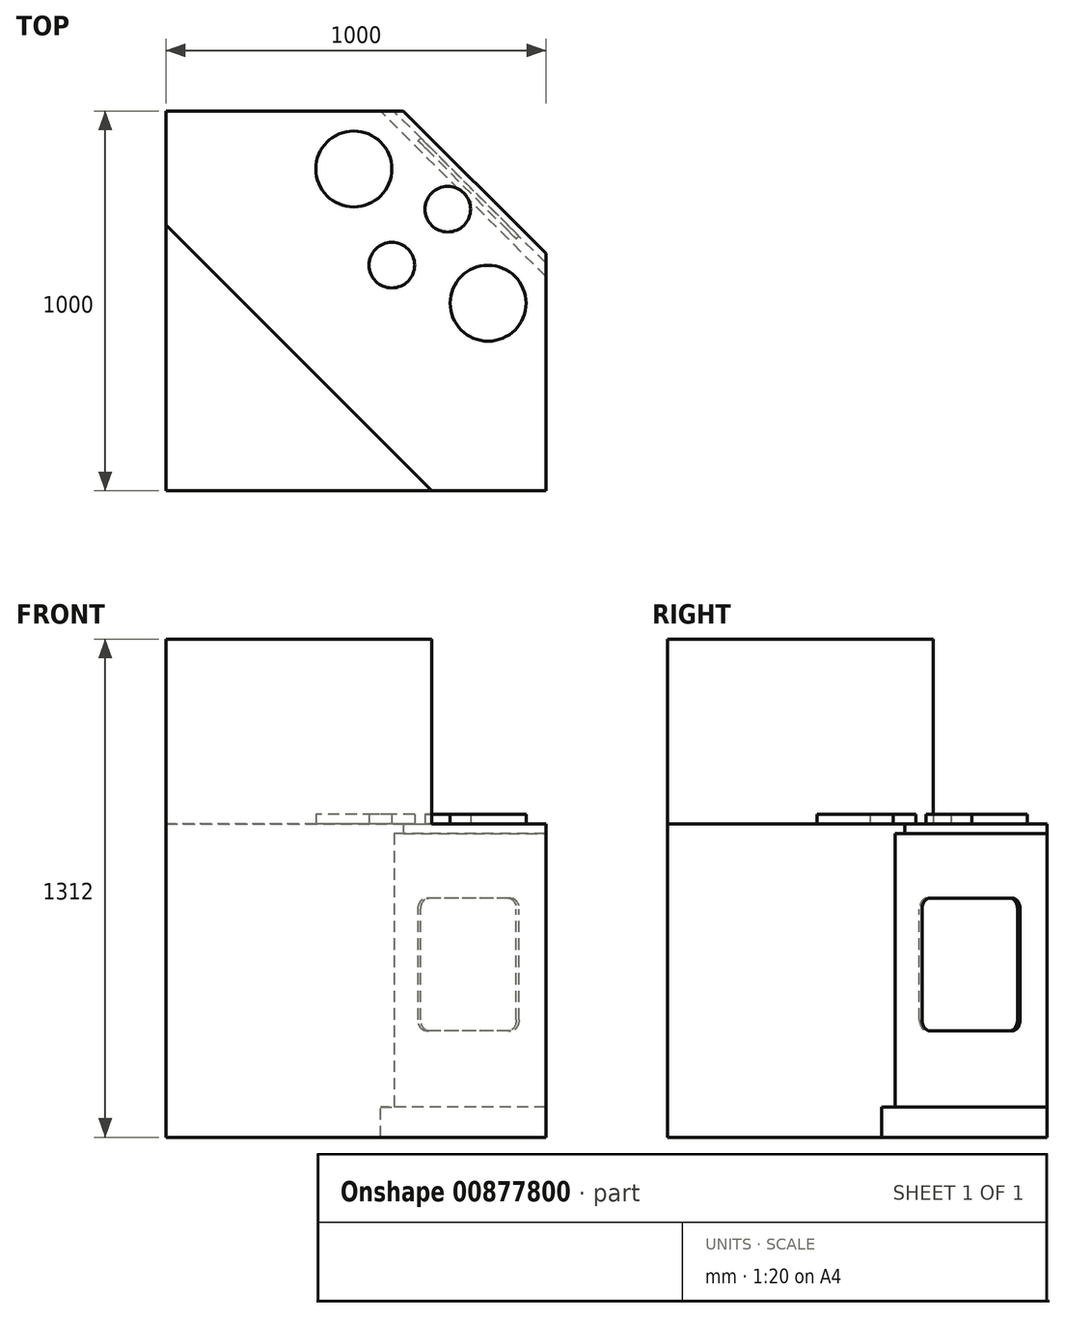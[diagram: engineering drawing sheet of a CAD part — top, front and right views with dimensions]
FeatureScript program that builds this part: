
annotation { "Feature Type Name" : "Feature", "Feature Type Description" : "" }
export const myFeature = defineFeature(function(context is Context, id is Id, definition is map)
    precondition{}
    {
        {
            var Q0;
            Q0=qCreatedBy(makeId("Top.planeOp"),FACE);
            var sketch = newSketch(context, id + "F0", { "sketchPlane" : qUnion([Q0])});
            skLineSegment(sketch, "E0.bottom", {"start": v(-500, -500) * mm, "end": v(500, -500) * mm});
            skLineSegment(sketch, "E0.left", {"start": v(-500, -500) * mm, "end": v(-500, 500) * mm});
            skPoint(sketch, "E0.middle", {"position": v(0, 0) * mm});
            skLineSegment(sketch, "E1", {"start": v(500, 100) * mm, "end": v(100, 500) * mm});
            skLineSegment(sketch, "E2", {"start": v(100, 500) * mm, "end": v(-500, 500) * mm});
            skLineSegment(sketch, "E3", {"start": v(500, 100) * mm, "end": v(500, -500) * mm});
            skSolve(sketch);
        }
        {
            var Q0;
            Q0 = qSketchRegion(id + "F0", true);
            extrude(context, id + "F1", {"entities" : qUnion([Q0]), "depth" : 800 * mm, "offsetDistance" : 25 * mm});
        }
        {
            var Q0;
            Q0=makeQuery(id+"F1.opExtrude","CAP_FACE",FACE,{"disambiguationData":[OSD([sQuery(id+"F0.wireOp",EDGE,"E0.bottom"),sQuery(id+"F0.wireOp",EDGE,"E0.left"),sQuery(id+"F0.wireOp",EDGE,"E1"),sQuery(id+"F0.wireOp",EDGE,"E2"),sQuery(id+"F0.wireOp",EDGE,"E3")])],"isStart":false});
            var sketch = newSketch(context, id + "F2", { "sketchPlane" : qUnion([Q0])});
            skLineSegment(sketch, "E4.bottom", {"start": v(-500, -500) * mm, "end": v(500, -500) * mm});
            skLineSegment(sketch, "E4.left", {"start": v(-500, -500) * mm, "end": v(-500, 500) * mm});
            skPoint(sketch, "E5", {"position": v(500, 125) * mm});
            skPoint(sketch, "E6", {"position": v(125, 500) * mm});
            skLineSegment(sketch, "E7", {"start": v(125, 500) * mm, "end": v(500, 125) * mm});
            skLineSegment(sketch, "E8", {"start": v(500, -500) * mm, "end": v(500, 125) * mm});
            skLineSegment(sketch, "E9", {"start": v(125, 500) * mm, "end": v(-500, 500) * mm});
            skSolve(sketch);
        }
        {
            var Q0;
            Q0 = qSketchRegion(id + "F2", true);
            extrude(context, id + "F3", {"entities" : qUnion([Q0]), "operationType" : NewBodyOperationType.ADD, "depth" : 25 * mm, "offsetDistance" : 25 * mm});
        }
        {
            var Q0;
            Q0=makeQuery(id+"F1.opExtrude","SWEPT_FACE",FACE,{"disambiguationData":[OSD([sQuery(id+"F0.wireOp",EDGE,"E1")])]});
            var sketch = newSketch(context, id + "F4", { "sketchPlane" : qUnion([Q0])});
            skLineSegment(sketch, "E10.bottom", {"start": v(-494.64, 0) * mm, "end": v(761.05, 0) * mm});
            skLineSegment(sketch, "E10.top", {"start": v(-494.64, 80) * mm, "end": v(761.05, 80) * mm});
            skLineSegment(sketch, "E10.left", {"start": v(-494.64, 0) * mm, "end": v(-494.64, 80) * mm});
            skLineSegment(sketch, "E10.right", {"start": v(761.05, 0) * mm, "end": v(761.05, 80) * mm});
            skSolve(sketch);
        }
        {
            var Q0;
            Q0 = qSketchRegion(id + "F4", true);
            extrude(context, id + "F5", {"entities" : qUnion([Q0]), "operationType" : NewBodyOperationType.REMOVE, "oppositeDirection" : true, "depth" : 25 * mm, "offsetDistance" : 25 * mm});
        }
        {
            var Q0;
            Q0=makeQuery(id+"F3.opExtrude","CAP_FACE",FACE,{"disambiguationData":[OSD([sQuery(id+"F2.wireOp",EDGE,"E4.bottom"),sQuery(id+"F2.wireOp",EDGE,"E4.left"),sQuery(id+"F2.wireOp",EDGE,"E7"),sQuery(id+"F2.wireOp",EDGE,"E8"),sQuery(id+"F2.wireOp",EDGE,"E9")])],"isStart":false});
            var sketch = newSketch(context, id + "F6", { "sketchPlane" : qUnion([Q0])});
            skCircle(sketch, "E11", {"center": v(241.79, 241.79) * mm, "radius": 60 * mm});
            skCircle(sketch, "E12", {"center": v(94.47, 94.47) * mm, "radius": 60 * mm});
            skCircle(sketch, "E13", {"center": v(347.86, -5.7) * mm, "radius": 100 * mm});
            skCircle(sketch, "E14", {"center": v(-5.7, 347.86) * mm, "radius": 100 * mm});
            skLineSegment(sketch, "E15", {"start": v(-500, -500) * mm, "end": v(312.5, 312.5) * mm, "construction": true});
            skSolve(sketch);
        }
        {
            var Q0;
            Q0 = qSketchRegion(id + "F6", true);
            extrude(context, id + "F7", {"entities" : qUnion([Q0]), "operationType" : NewBodyOperationType.ADD, "depth" : 25 * mm, "offsetDistance" : 25 * mm});
        }
        {
            var Q0;
            Q0=makeQuery(id+"F1.opExtrude","SWEPT_FACE",FACE,{"disambiguationData":[OSD([sQuery(id+"F0.wireOp",EDGE,"E1")])]});
            var sketch = newSketch(context, id + "F8", { "sketchPlane" : qUnion([Q0])});
            skLineSegment(sketch, "E16.bottom", {"start": v(-152.84, 280) * mm, "end": v(152.84, 280) * mm});
            skLineSegment(sketch, "E16.top", {"start": v(-152.84, 630) * mm, "end": v(152.84, 630) * mm});
            skLineSegment(sketch, "E16.left", {"start": v(-182.84, 310) * mm, "end": v(-182.84, 600) * mm});
            skLineSegment(sketch, "E16.right", {"start": v(182.84, 310) * mm, "end": v(182.84, 600) * mm});
            skPoint(sketch, "E17.visualSharp", {"position": v(182.84, 630) * mm});
            skArc(sketch, "E17.filletArc", {"start": v(182.84, 600) * mm, "mid": v(174.06, 621.21) * mm, "end": v(152.84, 630) * mm});
            skPoint(sketch, "E18.visualSharp", {"position": v(182.84, 280) * mm});
            skArc(sketch, "E18.filletArc", {"start": v(152.84, 280) * mm, "mid": v(174.06, 288.79) * mm, "end": v(182.84, 310) * mm});
            skPoint(sketch, "E19.visualSharp", {"position": v(-182.84, 280) * mm});
            skArc(sketch, "E19.filletArc", {"start": v(-182.84, 310) * mm, "mid": v(-174.06, 288.79) * mm, "end": v(-152.84, 280) * mm});
            skPoint(sketch, "E20.visualSharp", {"position": v(-182.84, 630) * mm});
            skArc(sketch, "E20.filletArc", {"start": v(-152.84, 630) * mm, "mid": v(-174.06, 621.21) * mm, "end": v(-182.84, 600) * mm});
            skSolve(sketch);
        }
        {
            var Q0;
            Q0 = qSketchRegion(id + "F8", true);
            extrude(context, id + "F9", {"entities" : qUnion([Q0]), "operationType" : NewBodyOperationType.REMOVE, "oppositeDirection" : true, "depth" : 10 * mm, "offsetDistance" : 25 * mm});
        }
        {
            var Q0;
            Q0=makeQuery(id+"F3.opExtrude","CAP_FACE",FACE,{"disambiguationData":[OSD([sQuery(id+"F2.wireOp",EDGE,"E4.bottom"),sQuery(id+"F2.wireOp",EDGE,"E4.left"),sQuery(id+"F2.wireOp",EDGE,"E7"),sQuery(id+"F2.wireOp",EDGE,"E8"),sQuery(id+"F2.wireOp",EDGE,"E9")])],"isStart":false});
            var sketch = newSketch(context, id + "F10", { "sketchPlane" : qUnion([Q0])});
            skLineSegment(sketch, "E21", {"start": v(-500, -500) * mm, "end": v(-500, 200) * mm});
            skLineSegment(sketch, "E22", {"start": v(-500, -500) * mm, "end": v(200, -500) * mm});
            skLineSegment(sketch, "E23", {"start": v(-500, 200) * mm, "end": v(200, -500) * mm});
            skSolve(sketch);
        }
        {
            var Q0;
            Q0 = qSketchRegion(id + "F10", true);
            extrude(context, id + "F11", {"entities" : qUnion([Q0]), "operationType" : NewBodyOperationType.ADD, "depth" : 487 * mm, "offsetDistance" : 25 * mm});
        }
    });
